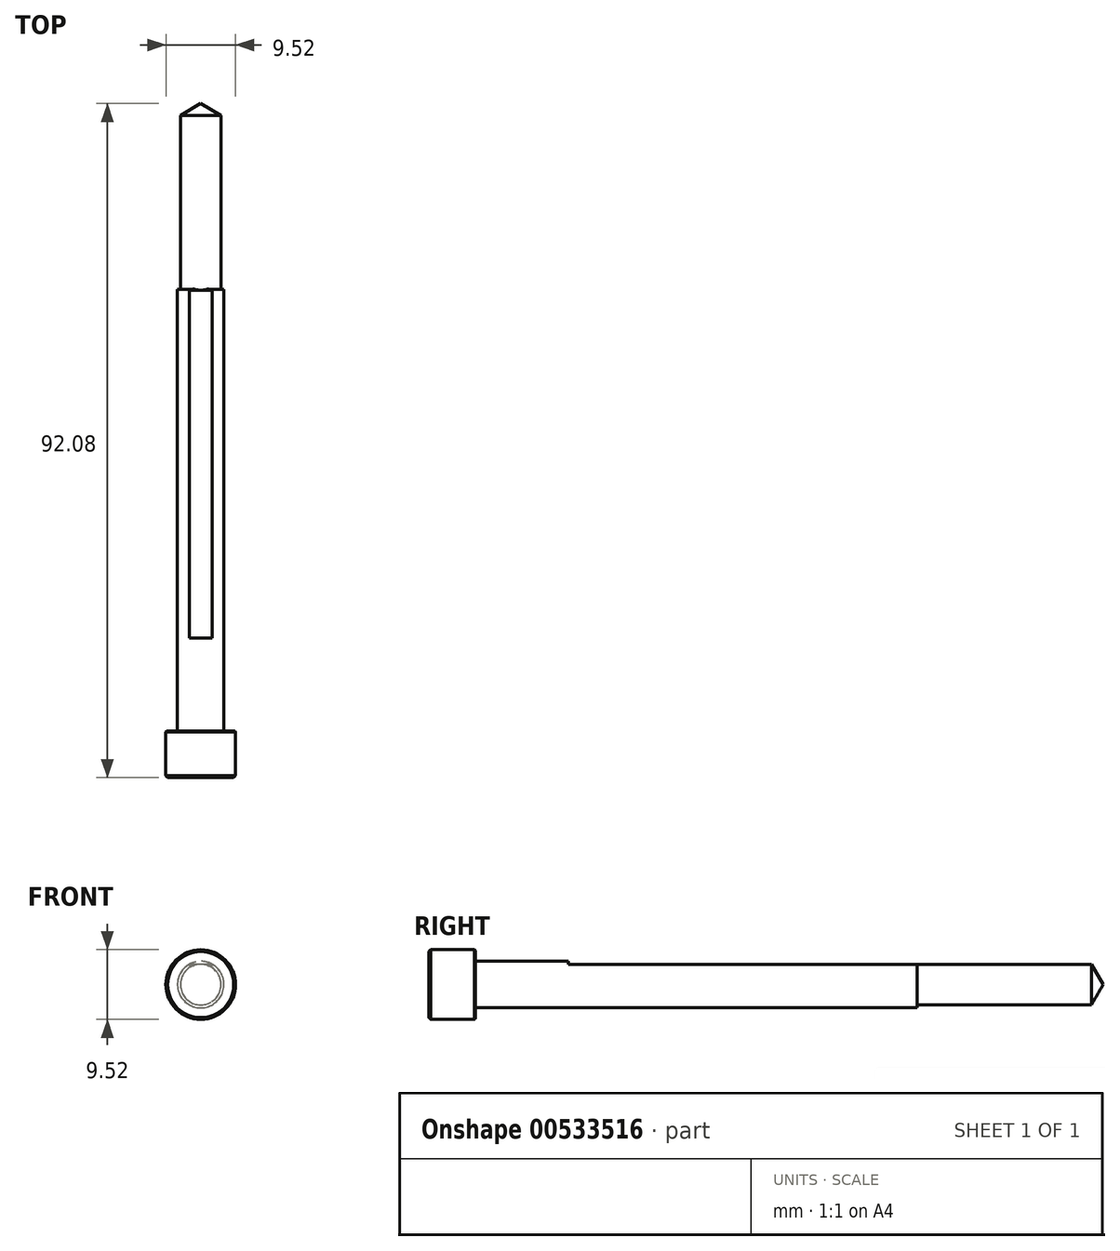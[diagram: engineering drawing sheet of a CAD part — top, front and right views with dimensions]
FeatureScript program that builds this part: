
annotation { "Feature Type Name" : "Feature", "Feature Type Description" : "" }
export const myFeature = defineFeature(function(context is Context, id is Id, definition is map)
    precondition{}
    {
        {
            var Q0;
            Q0=qCreatedBy(makeId("Right.planeOp"),FACE);
            var sketch = newSketch(context, id + "F0", { "sketchPlane" : qUnion([Q0])});
            skLineSegment(sketch, "E0", {"start": v(0, 0) * mm, "end": v(-85.73, 0) * mm});
            skLineSegment(sketch, "E1", {"start": v(0, 0) * mm, "end": v(-1.83, 3.18) * mm});
            skLineSegment(sketch, "E2", {"start": v(-1.83, 3.18) * mm, "end": v(-85.73, 3.17) * mm});
            skLineSegment(sketch, "E3", {"start": v(-85.73, 0) * mm, "end": v(-92.08, 0) * mm});
            skLineSegment(sketch, "E4.0", {"start": v(-85.73, 4.76) * mm, "end": v(-92.08, 4.76) * mm});
            skLineSegment(sketch, "E5", {"start": v(-85.73, 4.76) * mm, "end": v(-85.73, 3.17) * mm});
            skLineSegment(sketch, "E6", {"start": v(-92.08, 4.76) * mm, "end": v(-92.08, 0) * mm});
            skSolve(sketch);
        }
        {
            var Q0;
            Q0=makeQuery(id+"F0.imprint","IMPRINT",FACE,{"disambiguationData":[TD([[makeQuery(id+"F0.imprint","IMPRINT",EDGE,{"derivedFrom":sQuery(id+"F0.wireOp",EDGE,"E0")}),-1.0]])]});
            var Q1;
            Q1=sQuery(id+"F0.wireOp",EDGE,"E0");
            revolve(context, id + "F1", {"entities" : qUnion([Q0]), "axis" : qUnion([Q1]), "revolveType" : RevolveType.FULL});
        }
        {
            var Q0;
            Q0=qCreatedBy(makeId("Front.planeOp"),FACE);
            var sketch = newSketch(context, id + "F2", { "sketchPlane" : qUnion([Q0])});
            skCircle(sketch, "E7.0", {"center": v(0, 0) * mm, "radius": 4.76 * mm});
            skCircle(sketch, "E8.0", {"center": v(0, 0) * mm, "radius": 3.17 * mm});
            skLineSegment(sketch, "E9", {"start": v(0, 0) * mm, "end": v(0, 3.17) * mm, "construction": true});
            skLineSegment(sketch, "E10", {"start": v(0, 3.17) * mm, "end": v(4.35, 3.17) * mm});
            skLineSegment(sketch, "E11", {"start": v(4.35, 3.17) * mm, "end": v(4.35, 2.78) * mm});
            skLineSegment(sketch, "E12", {"start": v(4.35, 2.78) * mm, "end": v(0, 2.78) * mm});
            skLineSegment(sketch, "E13.MirrorCS", {"start": v(-4.35, 2.78) * mm, "end": v(0, 2.78) * mm});
            skLineSegment(sketch, "E14.MirrorCS", {"start": v(0, 3.17) * mm, "end": v(-4.35, 3.17) * mm});
            skLineSegment(sketch, "E15.MirrorCS", {"start": v(-4.35, 3.17) * mm, "end": v(-4.35, 2.78) * mm});
            skCircle(sketch, "E16", {"center": v(0, 0) * mm, "radius": 2.78 * mm});
            skSolve(sketch);
        }
        {
            var Q0;
            {var subQ2=sQuery(id+"F2.wireOp",EDGE,"E12");var subQ4=sQuery(id+"F2.wireOp",EDGE,"E13.MirrorCS");var subQ6=makeQuery(id+"F2.imprint","INTERSECT",VERTEX,{"derivedFrom":[subQ2,subQ4]});Q0=makeQuery(id+"F2.imprint","IMPRINT",FACE,{"disambiguationData":[TD([[makeQuery(id+"F2.imprint","IMPRINT",EDGE,{"disambiguationData":[TD([[subQ6,1.0]])],"derivedFrom":subQ2}),-1.0]])]});}
            var Q1;
            Q1=makeQuery(id+"F1.opRevolve","SWEPT_FACE",FACE,{"disambiguationData":[OSD([sQuery(id+"F0.wireOp",EDGE,"E5")])]});
            extrude(context, id + "F3", {"entities" : qUnion([Q0]), "operationType" : NewBodyOperationType.REMOVE, "endBound" : BoundingType.UP_TO_SURFACE, "depth" : 25.4 * mm, "endBoundEntityFace" : qUnion([Q1]), "hasOffset" : true, "offsetDistance" : 12.7 * mm});
        }
        {
            var Q0;
            {var subQ5=sQuery(id+"F2.wireOp",EDGE,"E16");Q0=makeQuery(id+"F2.imprint","IMPRINT",FACE,{"disambiguationData":[TD([[makeQuery(id+"F2.imprint","IMPRINT",EDGE,{"derivedFrom":subQ5}),-1.0]])]});}
            var Q1;
            {var subQ0=sQuery(id+"F2.wireOp",EDGE,"E8.0");var subQ2=sQuery(id+"F2.wireOp",EDGE,"E12");var subQ3=makeQuery(id+"F2.imprint","INTERSECT",VERTEX,{"derivedFrom":[subQ0,subQ2]});Q1=makeQuery(id+"F2.imprint","IMPRINT",FACE,{"disambiguationData":[TD([[makeQuery(id+"F2.imprint","IMPRINT",EDGE,{"disambiguationData":[TD([[subQ3,-1.0]])],"derivedFrom":subQ0}),1.0]])]});}
            extrude(context, id + "F4", {"entities" : qUnion([Q0, Q1]), "operationType" : NewBodyOperationType.REMOVE, "depth" : 25.4 * mm, "offsetDistance" : 25.4 * mm});
        }
        {
            var Q0;
            Q0=makeQuery(id+"F1.opRevolve","SWEPT_EDGE",EDGE,{"disambiguationData":[OSD([sQuery(id+"F0.wireOp",EDGE,"E4.0"),sQuery(id+"F0.wireOp",EDGE,"E6")])]});
            chamfer(context, id + "F5", {"entities" : qUnion([Q0]), "width" : 0.25 * mm, "tangentPropagation" : true});
        }
        {
            var Q0;
            Q0=makeQuery(id+"F1.opRevolve","SWEPT_EDGE",EDGE,{"disambiguationData":[OSD([sQuery(id+"F0.wireOp",EDGE,"E4.0"),sQuery(id+"F0.wireOp",EDGE,"E5")])]});
            var Q1;
            Q1=makeQuery(id+"F3.boolean.opBoolean","COPY",EDGE,{"derivedFrom":makeQuery(id+"F3.opExtrude","SWEPT_EDGE",EDGE,{"disambiguationData":[OSD([sQuery(id+"F2.wireOp",EDGE,"E8.0"),sQuery(id+"F2.wireOp",EDGE,"E13.MirrorCS")])]})});
            var Q2;
            Q2=makeQuery(id+"F3.boolean.opBoolean","COPY",EDGE,{"derivedFrom":makeQuery(id+"F3.opExtrude","CAP_EDGE",EDGE,{"disambiguationData":[OSD([sQuery(id+"F2.wireOp",EDGE,"E8.0")])],"isStart":false})});
            var Q3;
            Q3=makeQuery(id+"F3.boolean.opBoolean","COPY",EDGE,{"derivedFrom":makeQuery(id+"F3.opExtrude","SWEPT_EDGE",EDGE,{"disambiguationData":[OSD([sQuery(id+"F2.wireOp",EDGE,"E8.0"),sQuery(id+"F2.wireOp",EDGE,"E12")])]})});
            var Q4;
            Q4=makeQuery(id+"F4.boolean.opBoolean","INTERSECT",EDGE,{"disambiguationData":[OD(0.0)],"derivedFrom":[makeQuery(id+"F3.boolean.opBoolean","COPY",FACE,{"derivedFrom":makeQuery(id+"F3.opExtrude","SWEPT_FACE",FACE,{"disambiguationData":[OSD([sQuery(id+"F2.wireOp",EDGE,"E12"),sQuery(id+"F2.wireOp",EDGE,"E13.MirrorCS")])]})}),makeQuery(id+"F4.opExtrude","CAP_FACE",FACE,{"disambiguationData":[OSD([sQuery(id+"F2.wireOp",EDGE,"E8.0"),sQuery(id+"F2.wireOp",EDGE,"E16")])],"isStart":false})]});
            var Q5;
            Q5=makeQuery(id+"F4.boolean.opBoolean","INTERSECT",EDGE,{"disambiguationData":[OD(1.0)],"derivedFrom":[makeQuery(id+"F3.boolean.opBoolean","COPY",FACE,{"derivedFrom":makeQuery(id+"F3.opExtrude","SWEPT_FACE",FACE,{"disambiguationData":[OSD([sQuery(id+"F2.wireOp",EDGE,"E12"),sQuery(id+"F2.wireOp",EDGE,"E13.MirrorCS")])]})}),makeQuery(id+"F4.opExtrude","CAP_FACE",FACE,{"disambiguationData":[OSD([sQuery(id+"F2.wireOp",EDGE,"E8.0"),sQuery(id+"F2.wireOp",EDGE,"E16")])],"isStart":false})]});
            var Q6;
            Q6=makeQuery(id+"F4.boolean.opBoolean","COPY",EDGE,{"derivedFrom":makeQuery(id+"F4.opExtrude","CAP_EDGE",EDGE,{"disambiguationData":[OSD([sQuery(id+"F2.wireOp",EDGE,"E8.0")])],"isStart":false})});
            chamfer(context, id + "F6", {"entities" : qUnion([Q0, Q1, Q2, Q3, Q4, Q5, Q6]), "width" : 0.1 * mm, "tangentPropagation" : true});
        }
        {
            var Q0;
            Q0=makeQuery(id+"F1.opRevolve","SWEPT_EDGE",EDGE,{"disambiguationData":[OSD([sQuery(id+"F0.wireOp",EDGE,"E2"),sQuery(id+"F0.wireOp",EDGE,"E5")])]});
            fillet(context, id + "F7", {"entities" : qUnion([Q0]), "radius" : 0.25 * mm, "tangentPropagation" : true, "allowEdgeOverflow" : false});
        }
        {
            var Q0;
            Q0=makeQuery(id+"F4.boolean.opBoolean","COPY",EDGE,{"derivedFrom":makeQuery(id+"F4.opExtrude","CAP_EDGE",EDGE,{"disambiguationData":[OSD([sQuery(id+"F2.wireOp",EDGE,"E16")])],"isStart":false})});
            fillet(context, id + "F8", {"entities" : qUnion([Q0]), "radius" : 0.1 * mm, "tangentPropagation" : true, "allowEdgeOverflow" : false});
        }
    });
